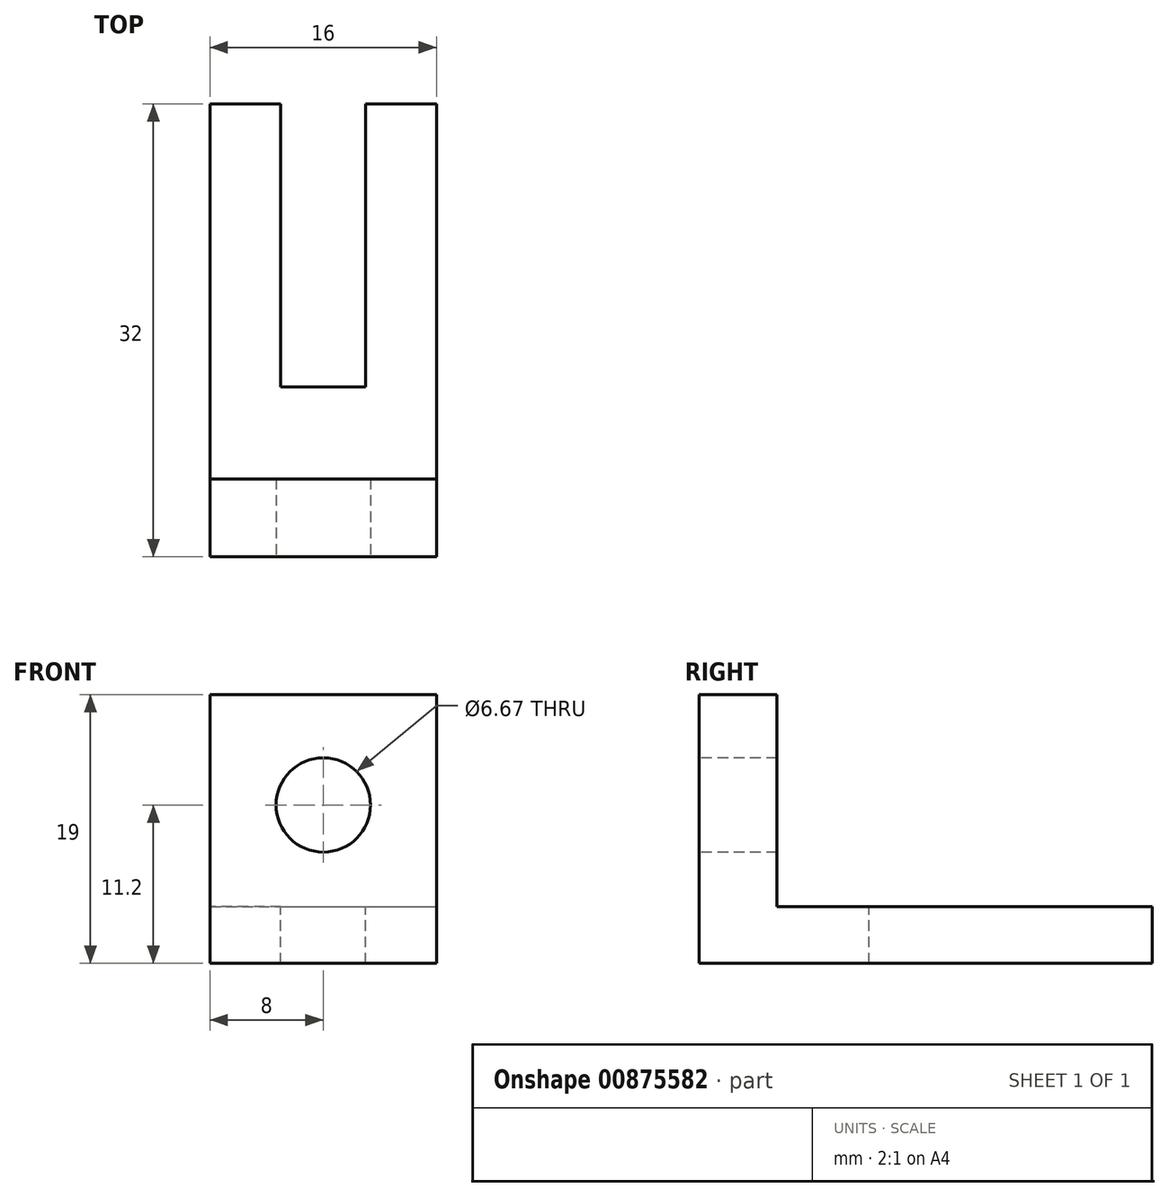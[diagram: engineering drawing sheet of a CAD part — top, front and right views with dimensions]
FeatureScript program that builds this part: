
annotation { "Feature Type Name" : "Feature", "Feature Type Description" : "" }
export const myFeature = defineFeature(function(context is Context, id is Id, definition is map)
    precondition{}
    {
        {
            var Q0;
            Q0=qCreatedBy(makeId("Top.planeOp"),FACE);
            var sketch = newSketch(context, id + "F0", { "sketchPlane" : qUnion([Q0])});
            skCircle(sketch, "E0", {"center": v(30.04, 22.5) * mm, "radius": 2.25 * mm});
            skCircle(sketch, "E1", {"center": v(30.04, -22.5) * mm, "radius": 2.25 * mm});
            skLineSegment(sketch, "E2.bottom", {"start": v(0, 0) * mm, "end": v(3, 0) * mm});
            skLineSegment(sketch, "E2.top", {"start": v(0, 32) * mm, "end": v(3, 32) * mm});
            skLineSegment(sketch, "E2.left", {"start": v(0, 0) * mm, "end": v(0, 32) * mm});
            skLineSegment(sketch, "E2.right", {"start": v(3, 0) * mm, "end": v(3, 32) * mm});
            skLineSegment(sketch, "E3.bottom", {"start": v(3, 32) * mm, "end": v(8, 32) * mm});
            skLineSegment(sketch, "E3.top", {"start": v(3, 0) * mm, "end": v(8, 0) * mm});
            skLineSegment(sketch, "E3.left", {"start": v(3, 32) * mm, "end": v(3, 0) * mm});
            skLineSegment(sketch, "E3.right", {"start": v(8, 32) * mm, "end": v(8, 0) * mm});
            skLineSegment(sketch, "E4", {"start": v(0, 12) * mm, "end": v(3, 12) * mm});
            skSolve(sketch);
        }
        {
            var Q0;
            {var subQ0=sQuery(id+"F0.wireOp",EDGE,"E2.bottom");Q0=makeQuery(id+"F0.imprint","IMPRINT",FACE,{"disambiguationData":[TD([[makeQuery(id+"F0.imprint","IMPRINT",EDGE,{"derivedFrom":subQ0}),1.0]])]});}
            var Q1;
            {var subQ3=sQuery(id+"F0.wireOp",EDGE,"E3.bottom");Q1=makeQuery(id+"F0.imprint","IMPRINT",FACE,{"disambiguationData":[TD([[makeQuery(id+"F0.imprint","IMPRINT",EDGE,{"derivedFrom":subQ3}),-1.0]])]});}
            extrude(context, id + "F1", {"entities" : qUnion([Q0, Q1]), "oppositeDirection" : true, "depth" : 4 * mm, "offsetDistance" : 25 * mm});
        }
        {
            var Q0;
            Q0=makeQuery(id+"F1.opExtrude","SWEPT_BODY",BODY,{"disambiguationData":[OSD([sQuery(id+"F0.wireOp",EDGE,"E2.bottom"),sQuery(id+"F0.wireOp",EDGE,"E2.left"),sQuery(id+"F0.wireOp",EDGE,"E3.bottom"),sQuery(id+"F0.wireOp",EDGE,"E3.top"),sQuery(id+"F0.wireOp",EDGE,"E3.left"),sQuery(id+"F0.wireOp",EDGE,"E3.right"),sQuery(id+"F0.wireOp",EDGE,"E4")])]});
            var Q1;
            Q1=makeQuery(id+"F1.opExtrude","SWEPT_FACE",FACE,{"disambiguationData":[OSD([sQuery(id+"F0.wireOp",EDGE,"E2.left")])]});
            mirror(context, id + "F2", {"operationType" : NewBodyOperationType.ADD, "entities" : qUnion([Q0]), "mirrorPlane" : qUnion([Q1])});
        }
        {
            var Q0;
            {var subQ0=makeQuery(id+"F1.opExtrude","CAP_FACE",FACE,{"disambiguationData":[OSD([sQuery(id+"F0.wireOp",EDGE,"E2.bottom"),sQuery(id+"F0.wireOp",EDGE,"E2.left"),sQuery(id+"F0.wireOp",EDGE,"E3.bottom"),sQuery(id+"F0.wireOp",EDGE,"E3.top"),sQuery(id+"F0.wireOp",EDGE,"E3.left"),sQuery(id+"F0.wireOp",EDGE,"E3.right"),sQuery(id+"F0.wireOp",EDGE,"E4")])],"isStart":true});Q0=makeQuery(id+"F2.boolean.opBoolean","MERGE",FACE,{"derivedFrom":[subQ0,makeQuery(id+"F2.opPattern","COPY",FACE,{"derivedFrom":subQ0,"instanceName":"1"})]});}
            var sketch = newSketch(context, id + "F3", { "sketchPlane" : qUnion([Q0])});
            skLineSegment(sketch, "E5", {"start": v(-8, 5.5) * mm, "end": v(8, 5.5) * mm});
            skSolve(sketch);
        }
        {
            var Q0;
            {var subQ0=sQuery(id+"F3.wireOp",EDGE,"E5");Q0=makeQuery(id+"F3.imprint","IMPRINT",FACE,{"disambiguationData":[TD([[makeQuery(id+"F3.imprint","IMPRINT",EDGE,{"derivedFrom":subQ0}),-1.0]])]});}
            extrude(context, id + "F4", {"entities" : qUnion([Q0]), "operationType" : NewBodyOperationType.ADD, "depth" : 15 * mm, "offsetDistance" : 25 * mm});
        }
        {
            var Q0;
            Q0=qCreatedBy(makeId("Front.planeOp"),FACE);
            var sketch = newSketch(context, id + "F5", { "sketchPlane" : qUnion([Q0])});
            skLineSegment(sketch, "E6.0", {"start": v(-3, -4) * mm, "end": v(-8, -4) * mm});
            skLineSegment(sketch, "E7.bottom", {"start": v(-3, -4) * mm, "end": v(0, -4) * mm});
            skLineSegment(sketch, "E7.top", {"start": v(-3, -46) * mm, "end": v(0, -46) * mm});
            skLineSegment(sketch, "E7.left", {"start": v(-3, -4) * mm, "end": v(-3, -46) * mm});
            skLineSegment(sketch, "E7.right", {"start": v(0, -4) * mm, "end": v(0, -46) * mm});
            skCircle(sketch, "E8", {"center": v(0, 7.2) * mm, "radius": 3.33 * mm});
            skSolve(sketch);
        }
        {
            var Q0;
            Q0=makeQuery(id+"F5.imprint","IMPRINT",FACE,{"disambiguationData":[TD([[makeQuery(id+"F5.imprint","IMPRINT",EDGE,{"derivedFrom":sQuery(id+"F5.wireOp",EDGE,"E8")}),1.0]])]});
            extrude(context, id + "F6", {"entities" : qUnion([Q0]), "operationType" : NewBodyOperationType.REMOVE, "endBound" : BoundingType.THROUGH_ALL, "oppositeDirection" : true, "depth" : 25 * mm, "offsetDistance" : 25 * mm});
        }
    });
